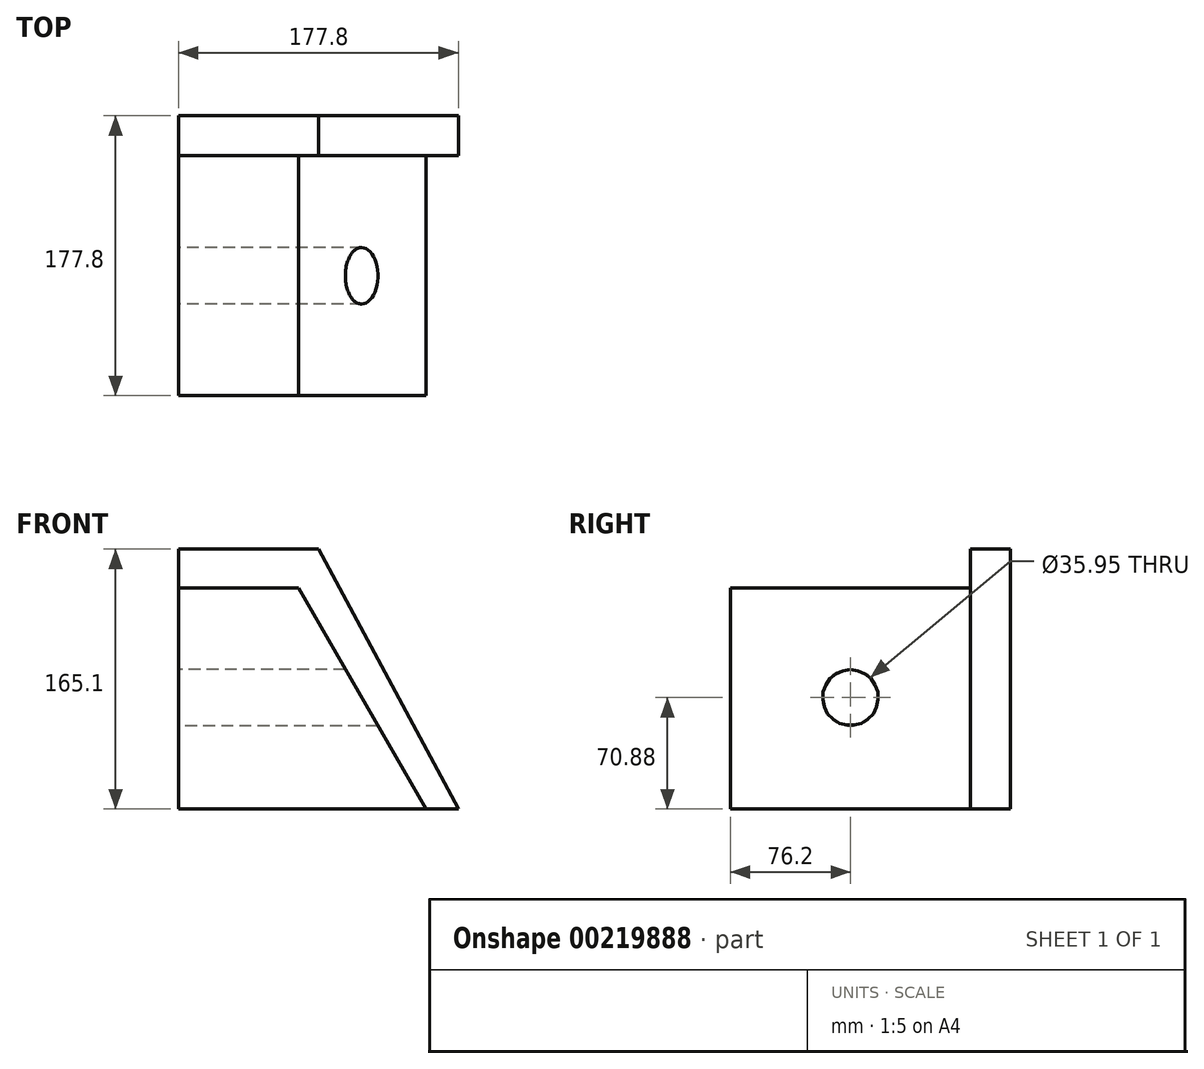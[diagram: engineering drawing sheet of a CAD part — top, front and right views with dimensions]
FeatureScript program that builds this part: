
annotation { "Feature Type Name" : "Feature", "Feature Type Description" : "" }
export const myFeature = defineFeature(function(context is Context, id is Id, definition is map)
    precondition{}
    {
        {
            var Q0;
            Q0=qCreatedBy(makeId("Front.planeOp"),FACE);
            var sketch = newSketch(context, id + "F0", { "sketchPlane" : qUnion([Q0])});
            skLineSegment(sketch, "E0", {"start": v(0, 0) * mm, "end": v(-177.8, 0) * mm});
            skLineSegment(sketch, "E1", {"start": v(-177.8, 0) * mm, "end": v(-177.8, 165.1) * mm});
            skLineSegment(sketch, "E2", {"start": v(-177.8, 165.1) * mm, "end": v(-88.9, 165.1) * mm});
            skLineSegment(sketch, "E3", {"start": v(-88.9, 165.1) * mm, "end": v(0, 0) * mm});
            skSolve(sketch);
        }
        {
            var Q0;
            Q0 = qSketchRegion(id + "F0", true);
            extrude(context, id + "F1", {"entities" : qUnion([Q0]), "depth" : 25.4 * mm});
        }
        {
            var Q0;
            Q0=makeQuery(id+"F1.opExtrude","CAP_FACE",FACE,{"disambiguationData":[OSD([sQuery(id+"F0.wireOp",EDGE,"E0"),sQuery(id+"F0.wireOp",EDGE,"E1"),sQuery(id+"F0.wireOp",EDGE,"E2"),sQuery(id+"F0.wireOp",EDGE,"E3")])],"isStart":false});
            var sketch = newSketch(context, id + "F2", { "sketchPlane" : qUnion([Q0])});
            skLineSegment(sketch, "E4", {"start": v(-177.8, 0) * mm, "end": v(-177.8, 140.42) * mm});
            skLineSegment(sketch, "E5", {"start": v(-177.8, 140.42) * mm, "end": v(-101.62, 140.42) * mm});
            skLineSegment(sketch, "E6", {"start": v(-101.62, 140.42) * mm, "end": v(-20.45, 0) * mm});
            skLineSegment(sketch, "E7", {"start": v(-20.45, 0) * mm, "end": v(-177.8, 0) * mm});
            skSolve(sketch);
        }
        {
            var Q0;
            Q0 = qSketchRegion(id + "F2", true);
            extrude(context, id + "F3", {"entities" : qUnion([Q0]), "operationType" : NewBodyOperationType.ADD, "depth" : 152.4 * mm});
        }
        {
            var Q0;
            Q0=makeQuery(id+"F3.boolean.opBoolean","MERGE",FACE,{"derivedFrom":[makeQuery(id+"F1.opExtrude","SWEPT_FACE",FACE,{"disambiguationData":[OSD([sQuery(id+"F0.wireOp",EDGE,"E1")])]}),makeQuery(id+"F3.opExtrude","SWEPT_FACE",FACE,{"disambiguationData":[OSD([sQuery(id+"F2.wireOp",EDGE,"E4")])]})]});
            var sketch = newSketch(context, id + "F4", { "sketchPlane" : qUnion([Q0])});
            skCircle(sketch, "E8", {"center": v(101.6, 70.88) * mm, "radius": 17.98 * mm});
            skPoint(sketch, "E8.centerSnap0", {"position": v(101.6, 140.42) * mm});
            skSolve(sketch);
        }
        {
            var Q0;
            Q0 = qSketchRegion(id + "F4", true);
            extrude(context, id + "F5", {"entities" : qUnion([Q0]), "operationType" : NewBodyOperationType.REMOVE, "endBound" : BoundingType.THROUGH_ALL, "oppositeDirection" : true, "depth" : 25.4 * mm});
        }
    });
